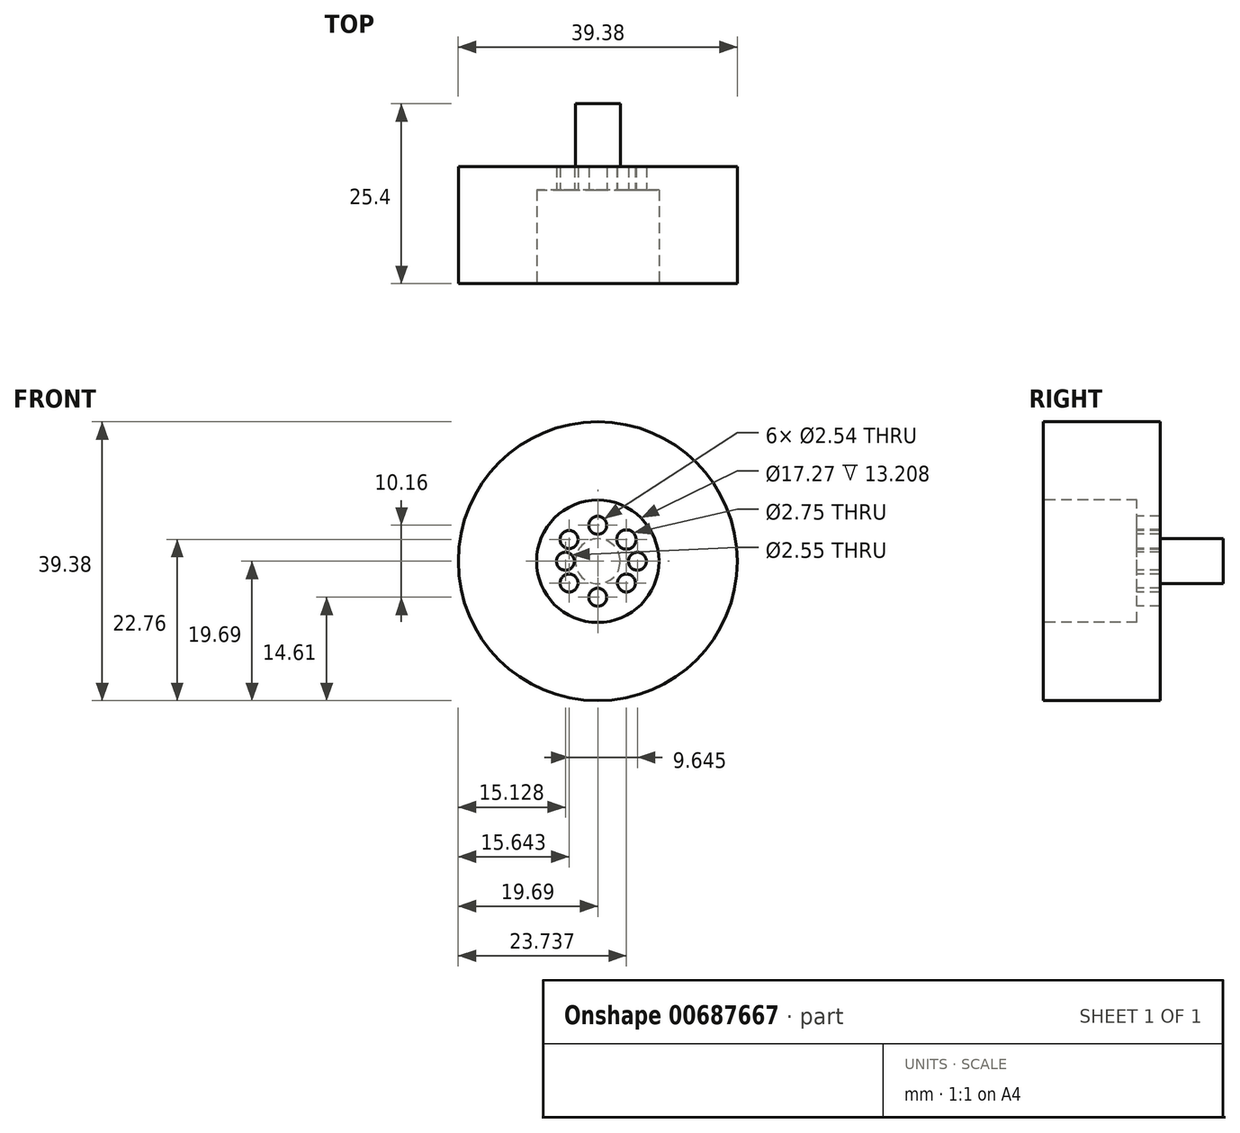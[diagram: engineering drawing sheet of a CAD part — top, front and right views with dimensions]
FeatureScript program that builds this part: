
annotation { "Feature Type Name" : "Feature", "Feature Type Description" : "" }
export const myFeature = defineFeature(function(context is Context, id is Id, definition is map)
    precondition{}
    {
        {
            var Q0;
            Q0=qCreatedBy(makeId("Front.planeOp"),FACE);
            var sketch = newSketch(context, id + "F0", { "sketchPlane" : qUnion([Q0])});
            skCircle(sketch, "E0", {"center": v(0, 0) * mm, "radius": 19.69 * mm});
            skSolve(sketch);
        }
        {
            var Q0;
            Q0 = qSketchRegion(id + "F0", true);
            extrude(context, id + "F1", {"entities" : qUnion([Q0]), "oppositeDirection" : true, "depth" : 16.5 * mm, "offsetDistance" : 25.4 * mm});
        }
        {
            var Q0;
            Q0=qCreatedBy(makeId("Front.planeOp"),FACE);
            var sketch = newSketch(context, id + "F2", { "sketchPlane" : qUnion([Q0])});
            skCircle(sketch, "E1", {"center": v(0, 0) * mm, "radius": 8.64 * mm});
            skSolve(sketch);
        }
        {
            var Q0;
            Q0 = qSketchRegion(id + "F2", true);
            extrude(context, id + "F3", {"entities" : qUnion([Q0]), "operationType" : NewBodyOperationType.REMOVE, "oppositeDirection" : true, "depth" : 13.2 * mm, "offsetDistance" : 25.4 * mm});
        }
        {
            var Q0;
            Q0=makeQuery(id+"F1.opExtrude","CAP_FACE",FACE,{"disambiguationData":[OSD([sQuery(id+"F0.wireOp",EDGE,"E0")])],"isStart":false});
            var sketch = newSketch(context, id + "F4", { "sketchPlane" : qUnion([Q0])});
            skCircle(sketch, "E2", {"center": v(0, 0) * mm, "radius": 3.18 * mm});
            skSolve(sketch);
        }
        {
            var Q0;
            Q0 = qSketchRegion(id + "F4", true);
            extrude(context, id + "F5", {"entities" : qUnion([Q0]), "operationType" : NewBodyOperationType.ADD, "depth" : 8.9 * mm, "offsetDistance" : 25.4 * mm});
        }
        {
            var Q0;
            Q0=makeQuery(id+"F3.boolean.opBoolean","COPY",FACE,{"derivedFrom":makeQuery(id+"F3.opExtrude","CAP_FACE",FACE,{"disambiguationData":[OSD([sQuery(id+"F2.wireOp",EDGE,"E1")])],"isStart":false})});
            var sketch = newSketch(context, id + "F6", { "sketchPlane" : qUnion([Q0])});
            skLineSegment(sketch, "E3", {"start": v(0, 0) * mm, "end": v(-4.05, 3.07) * mm});
            skLineSegment(sketch, "E4", {"start": v(-4.05, 3.07) * mm, "end": v(4.05, -3.07) * mm});
            skLineSegment(sketch, "E5", {"start": v(4.05, -3.07) * mm, "end": v(0, 0) * mm});
            skLineSegment(sketch, "E6", {"start": v(0, 0) * mm, "end": v(-4.05, -3.07) * mm});
            skLineSegment(sketch, "E7", {"start": v(-4.05, -3.07) * mm, "end": v(4.05, 3.07) * mm});
            skLineSegment(sketch, "E8", {"start": v(4.05, 3.07) * mm, "end": v(0, 0) * mm});
            skLineSegment(sketch, "E9", {"start": v(0, 0) * mm, "end": v(0, 5.08) * mm});
            skLineSegment(sketch, "E10", {"start": v(0, 5.08) * mm, "end": v(0, -5.08) * mm});
            skLineSegment(sketch, "E11", {"start": v(0, -5.08) * mm, "end": v(0, 0) * mm});
            skLineSegment(sketch, "E12", {"start": v(-4.56, 0) * mm, "end": v(5.6, 0) * mm});
            skCircle(sketch, "E13", {"center": v(0, 5.08) * mm, "radius": 1.27 * mm});
            skCircle(sketch, "E14", {"center": v(4.05, 3.07) * mm, "radius": 1.37 * mm});
            skCircle(sketch, "E15", {"center": v(5.6, 0) * mm, "radius": 1.27 * mm});
            skCircle(sketch, "E16", {"center": v(4.05, -3.07) * mm, "radius": 1.27 * mm});
            skCircle(sketch, "E17", {"center": v(0, -5.08) * mm, "radius": 1.27 * mm});
            skCircle(sketch, "E18", {"center": v(-4.05, -3.07) * mm, "radius": 1.27 * mm});
            skCircle(sketch, "E19", {"center": v(-4.56, 0) * mm, "radius": 1.27 * mm});
            skCircle(sketch, "E20", {"center": v(-4.05, 3.07) * mm, "radius": 1.27 * mm});
            skSolve(sketch);
        }
        {
            var Q0;
            Q0=makeQuery(id+"F6.imprint","IMPRINT",FACE,{"disambiguationData":[TD([[makeQuery(id+"F6.imprint","IMPRINT",EDGE,{"derivedFrom":sQuery(id+"F6.wireOp",EDGE,"E14")}),1.0]])]});
            var Q1;
            Q1=makeQuery(id+"F6.imprint","IMPRINT",FACE,{"disambiguationData":[TD([[makeQuery(id+"F6.imprint","IMPRINT",EDGE,{"derivedFrom":sQuery(id+"F6.wireOp",EDGE,"E15")}),1.0]])]});
            var Q2;
            Q2=makeQuery(id+"F6.imprint","IMPRINT",FACE,{"disambiguationData":[TD([[makeQuery(id+"F6.imprint","IMPRINT",EDGE,{"derivedFrom":sQuery(id+"F6.wireOp",EDGE,"E16")}),1.0]])]});
            var Q3;
            Q3=makeQuery(id+"F6.imprint","IMPRINT",FACE,{"disambiguationData":[TD([[makeQuery(id+"F6.imprint","IMPRINT",EDGE,{"derivedFrom":sQuery(id+"F6.wireOp",EDGE,"E18")}),1.0]])]});
            var Q4;
            Q4=makeQuery(id+"F6.imprint","IMPRINT",FACE,{"disambiguationData":[TD([[makeQuery(id+"F6.imprint","IMPRINT",EDGE,{"derivedFrom":sQuery(id+"F6.wireOp",EDGE,"E17")}),1.0]])]});
            var Q5;
            Q5=makeQuery(id+"F6.imprint","IMPRINT",FACE,{"disambiguationData":[TD([[makeQuery(id+"F6.imprint","IMPRINT",EDGE,{"derivedFrom":sQuery(id+"F6.wireOp",EDGE,"E19")}),1.0]])]});
            var Q6;
            Q6=makeQuery(id+"F6.imprint","IMPRINT",FACE,{"disambiguationData":[TD([[makeQuery(id+"F6.imprint","IMPRINT",EDGE,{"derivedFrom":sQuery(id+"F6.wireOp",EDGE,"E20")}),1.0]])]});
            var Q7;
            Q7=makeQuery(id+"F6.imprint","IMPRINT",FACE,{"disambiguationData":[TD([[makeQuery(id+"F6.imprint","IMPRINT",EDGE,{"derivedFrom":sQuery(id+"F6.wireOp",EDGE,"E13")}),1.0]])]});
            extrude(context, id + "F7", {"entities" : qUnion([Q0, Q1, Q2, Q3, Q4, Q5, Q6, Q7]), "operationType" : NewBodyOperationType.REMOVE, "oppositeDirection" : true, "depth" : 25.4 * mm, "offsetDistance" : 25.4 * mm});
        }
    });
